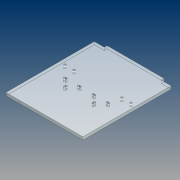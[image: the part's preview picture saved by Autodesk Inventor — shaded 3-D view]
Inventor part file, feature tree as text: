
AUTODESK INVENTOR PART (.ipt)
format: ipt  version: 2021 (Build 250183000, 183)  size: 190,976 bytes
history: native  units: mm
features: other x10, reference x8, extrude x3, sketch x3, projected_geometry x1
ambient origin geometry x8: Origin, YZ Plane, XZ Plane, XY Plane, X Axis, Y Axis, Z Axis, Center Point
bodies: Solid1 (feature_tree)
feature tree (25):
  extrude  "Extrusion1"  Depth=320.0mm
  extrude  "Extrusion2"  Depth=10.0mm TaperAngle=0.0deg
  extrude  "Extrusion3"  Depth=200.0mm
  sketch  "Sketch1"  dims[d0=270.0mm d1=320.0mm]
  sketch  "Sketch2"  dims[d2=10.0mm d3=0.0mm d4=10.0mm d5=0.0mm]
  reference  "Reference1"
  reference  "Reference2"
  reference  "Reference3"
  reference  "Reference4"
  reference  "Reference5"
  reference  "Reference6"
  reference  "Reference7"
  reference  "Reference8"
  sketch  "Sketch3"  dims[d6=10.0mm d7=200.0mm d8=49.25mm d9=0.0mm]
  projected_geometry  "Projected Loop1"
  other  "0002_ASS_Ban_lap_ghep_Wood_01.iam"
  other  "0002_Tam_nguyen_Truc_Z:1"
  other  "ke-nhom-noi-2020:4"
  other  "ke-nhom-noi-2020:5"
  other  "ke-nhom-noi-2020:3"
  other  "ke-nhom-noi-2020:6"
  other  "ke-nhom-noi-2020:2"
  other  "ke-nhom-noi-2020:1"
  other  "SHF8:2"
  other  "SHF8:1"
